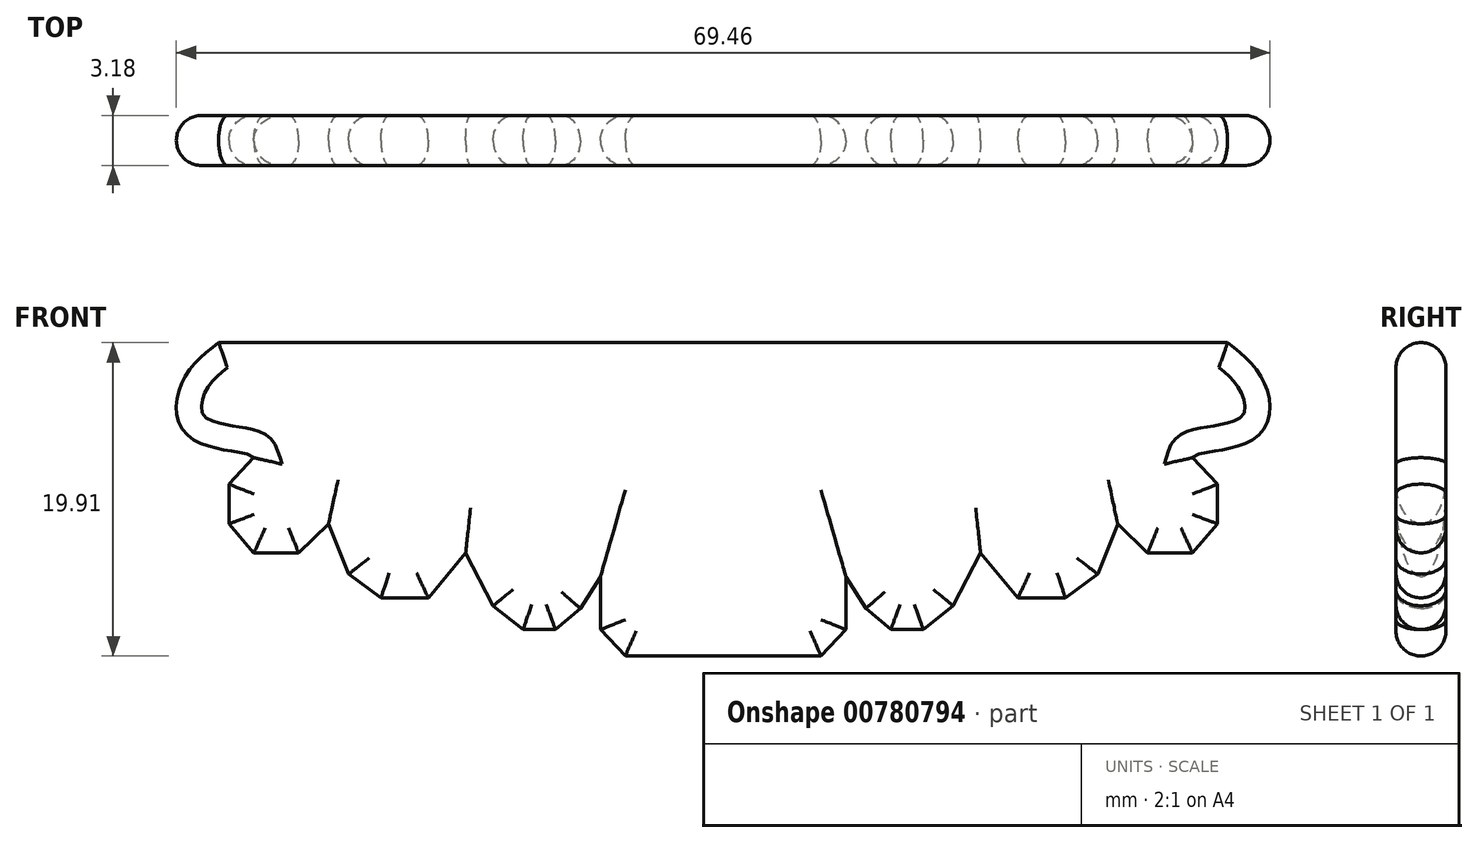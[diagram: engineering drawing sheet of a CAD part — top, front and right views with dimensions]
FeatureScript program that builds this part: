
annotation { "Feature Type Name" : "Feature", "Feature Type Description" : "" }
export const myFeature = defineFeature(function(context is Context, id is Id, definition is map)
    precondition{}
    {
        {
            var Q0;
            Q0=qCreatedBy(makeId("Front.planeOp"),FACE);
            var sketch = newSketch(context, id + "F0", { "sketchPlane" : qUnion([Q0])});
            skLineSegment(sketch, "E0", {"start": v(222.2, -107.52) * mm, "end": v(222.2, 203.58) * mm});
            skLineSegment(sketch, "E1", {"start": v(222.2, 203.58) * mm, "end": v(149.6, 203.58) * mm});
            skLineSegment(sketch, "E2", {"start": v(149.6, 203.58) * mm, "end": v(-239.67, 203.58) * mm});
            skFitSpline(sketch, "E3", {"points": [v(-239.67, 203.58) * mm, v(-277.43, 161.87) * mm, v(-269.83, 108.1) * mm, v(-206.49, 89.28) * mm, v(-203.96, 86.59) * mm], "startDerivative": vector(-149.5, -118.64) * mm, "endDerivative": vector(11.53, -36.45) * mm});
            skLineSegment(sketch, "E4", {"start": v(-203.96, 86.59) * mm, "end": v(-229.3, 59.7) * mm});
            skLineSegment(sketch, "E5", {"start": v(-229.3, 59.7) * mm, "end": v(-229.3, 19.38) * mm});
            skLineSegment(sketch, "E6", {"start": v(-229.3, 19.38) * mm, "end": v(-203.96, -10.2) * mm});
            skLineSegment(sketch, "E7", {"start": v(-203.96, -10.2) * mm, "end": v(-158.35, -10.2) * mm});
            skLineSegment(sketch, "E8", {"start": v(-158.35, -10.2) * mm, "end": v(-127.95, 19.38) * mm});
            skLineSegment(sketch, "E9", {"start": v(-127.95, 19.38) * mm, "end": v(-107.68, -31.7) * mm});
            skLineSegment(sketch, "E10", {"start": v(-107.68, -31.7) * mm, "end": v(-74.74, -55.9) * mm});
            skLineSegment(sketch, "E11", {"start": v(-74.74, -55.9) * mm, "end": v(-26.6, -55.9) * mm});
            skLineSegment(sketch, "E12", {"start": v(-26.6, -55.9) * mm, "end": v(11.4, -10.2) * mm});
            skLineSegment(sketch, "E13", {"start": v(11.4, -10.2) * mm, "end": v(39.28, -63.97) * mm});
            skLineSegment(sketch, "E14", {"start": v(39.28, -63.97) * mm, "end": v(69.68, -88.16) * mm});
            skLineSegment(sketch, "E15", {"start": v(69.68, -88.16) * mm, "end": v(102.62, -88.16) * mm});
            skLineSegment(sketch, "E16", {"start": v(102.62, -88.16) * mm, "end": v(127.95, -66.66) * mm});
            skLineSegment(sketch, "E17", {"start": v(127.95, -66.66) * mm, "end": v(148.22, -34.4) * mm});
            skLineSegment(sketch, "E18", {"start": v(148.22, -34.4) * mm, "end": v(148.22, -88.16) * mm});
            skLineSegment(sketch, "E19", {"start": v(148.22, -88.16) * mm, "end": v(173.56, -115.05) * mm});
            skLineSegment(sketch, "E20", {"start": v(173.56, -115.05) * mm, "end": v(222.2, -115.05) * mm});
            skLineSegment(sketch, "E21", {"start": v(222.2, -115.05) * mm, "end": v(222.2, 203.58) * mm});
            skSolve(sketch);
        }
        {
            var Q0;
            {var subQ0=sQuery(id+"F0.wireOp",EDGE,"E1");Q0=makeQuery(id+"F0.imprint","IMPRINT",FACE,{"disambiguationData":[TD([[makeQuery(id+"F0.imprint","IMPRINT",EDGE,{"derivedFrom":subQ0}),1.0]])]});}
            extrude(context, id + "F1", {"entities" : qUnion([Q0]), "depth" : 50.8 * mm, "offsetDistance" : 25.4 * mm});
        }
        {
            var Q0;
            Q0=makeQuery(id+"F1.opExtrude","SWEPT_FACE",FACE,{"disambiguationData":[OSD([sQuery(id+"F0.wireOp",EDGE,"E21")])]});
            var sketch = newSketch(context, id + "F2", { "sketchPlane" : qUnion([Q0])});
            skLineSegment(sketch, "E22", {"start": v(-50.8, 203.58) * mm, "end": v(-50.8, -115.05) * mm});
            skLineSegment(sketch, "E23", {"start": v(-50.8, -115.05) * mm, "end": v(0, -115.05) * mm});
            skLineSegment(sketch, "E24", {"start": v(0, -115.05) * mm, "end": v(0, 203.58) * mm});
            skLineSegment(sketch, "E25", {"start": v(0, 203.58) * mm, "end": v(-50.8, 203.58) * mm});
            skSolve(sketch);
        }
        {
            var Q0;
            Q0=makeQuery(id+"F2.imprint","IMPRINT",FACE,{"disambiguationData":[TD([[makeQuery(id+"F2.imprint","IMPRINT",EDGE,{"derivedFrom":sQuery(id+"F2.wireOp",EDGE,"E22")}),-1.0]])]});
            extrude(context, id + "F3", {"entities" : qUnion([Q0]), "operationType" : NewBodyOperationType.ADD, "depth" : 50.8 * mm, "offsetDistance" : 25.4 * mm});
        }
        {
            var Q0;
            Q0=makeQuery(id+"F3.boolean.opBoolean","MERGE",EDGE,{"derivedFrom":[makeQuery(id+"F1.opExtrude","CAP_EDGE",EDGE,{"disambiguationData":[OSD([sQuery(id+"F0.wireOp",EDGE,"E1"),sQuery(id+"F0.wireOp",EDGE,"E2")])],"isStart":false}),makeQuery(id+"F3.opExtrude","SWEPT_EDGE",EDGE,{"disambiguationData":[OSD([sQuery(id+"F2.wireOp",EDGE,"E22"),sQuery(id+"F2.wireOp",EDGE,"E25")])]})]});
            var Q1;
            Q1=makeQuery(id+"F1.opExtrude","CAP_EDGE",EDGE,{"disambiguationData":[OSD([sQuery(id+"F0.wireOp",EDGE,"E3")])],"isStart":false});
            var Q2;
            Q2=makeQuery(id+"F1.opExtrude","CAP_EDGE",EDGE,{"disambiguationData":[OSD([sQuery(id+"F0.wireOp",EDGE,"E4")])],"isStart":false});
            var Q3;
            Q3=makeQuery(id+"F1.opExtrude","CAP_EDGE",EDGE,{"disambiguationData":[OSD([sQuery(id+"F0.wireOp",EDGE,"E5")])],"isStart":false});
            var Q4;
            Q4=makeQuery(id+"F1.opExtrude","CAP_EDGE",EDGE,{"disambiguationData":[OSD([sQuery(id+"F0.wireOp",EDGE,"E6")])],"isStart":false});
            var Q5;
            Q5=makeQuery(id+"F1.opExtrude","CAP_EDGE",EDGE,{"disambiguationData":[OSD([sQuery(id+"F0.wireOp",EDGE,"E8")])],"isStart":false});
            var Q6;
            Q6=makeQuery(id+"F1.opExtrude","CAP_EDGE",EDGE,{"disambiguationData":[OSD([sQuery(id+"F0.wireOp",EDGE,"E7")])],"isStart":false});
            var Q7;
            Q7=makeQuery(id+"F1.opExtrude","CAP_EDGE",EDGE,{"disambiguationData":[OSD([sQuery(id+"F0.wireOp",EDGE,"E9")])],"isStart":false});
            var Q8;
            Q8=makeQuery(id+"F1.opExtrude","CAP_EDGE",EDGE,{"disambiguationData":[OSD([sQuery(id+"F0.wireOp",EDGE,"E10")])],"isStart":false});
            var Q9;
            Q9=makeQuery(id+"F1.opExtrude","CAP_EDGE",EDGE,{"disambiguationData":[OSD([sQuery(id+"F0.wireOp",EDGE,"E11")])],"isStart":false});
            var Q10;
            Q10=makeQuery(id+"F1.opExtrude","CAP_EDGE",EDGE,{"disambiguationData":[OSD([sQuery(id+"F0.wireOp",EDGE,"E12")])],"isStart":false});
            var Q11;
            Q11=makeQuery(id+"F1.opExtrude","CAP_EDGE",EDGE,{"disambiguationData":[OSD([sQuery(id+"F0.wireOp",EDGE,"E13")])],"isStart":false});
            var Q12;
            Q12=makeQuery(id+"F1.opExtrude","CAP_EDGE",EDGE,{"disambiguationData":[OSD([sQuery(id+"F0.wireOp",EDGE,"E14")])],"isStart":false});
            var Q13;
            Q13=makeQuery(id+"F1.opExtrude","CAP_EDGE",EDGE,{"disambiguationData":[OSD([sQuery(id+"F0.wireOp",EDGE,"E15")])],"isStart":false});
            var Q14;
            Q14=makeQuery(id+"F1.opExtrude","CAP_EDGE",EDGE,{"disambiguationData":[OSD([sQuery(id+"F0.wireOp",EDGE,"E16")])],"isStart":false});
            var Q15;
            Q15=makeQuery(id+"F3.boolean.opBoolean","MERGE",EDGE,{"derivedFrom":[makeQuery(id+"F1.opExtrude","CAP_EDGE",EDGE,{"disambiguationData":[OSD([sQuery(id+"F0.wireOp",EDGE,"E20")])],"isStart":false}),makeQuery(id+"F3.opExtrude","SWEPT_EDGE",EDGE,{"disambiguationData":[OSD([sQuery(id+"F2.wireOp",EDGE,"E22"),sQuery(id+"F2.wireOp",EDGE,"E23")])]})]});
            var Q16;
            Q16=makeQuery(id+"F1.opExtrude","CAP_EDGE",EDGE,{"disambiguationData":[OSD([sQuery(id+"F0.wireOp",EDGE,"E19")])],"isStart":false});
            var Q17;
            Q17=makeQuery(id+"F1.opExtrude","CAP_EDGE",EDGE,{"disambiguationData":[OSD([sQuery(id+"F0.wireOp",EDGE,"E18")])],"isStart":false});
            var Q18;
            Q18=makeQuery(id+"F1.opExtrude","CAP_EDGE",EDGE,{"disambiguationData":[OSD([sQuery(id+"F0.wireOp",EDGE,"E17")])],"isStart":false});
            fillet(context, id + "F4", {"entities" : qUnion([Q0, Q1, Q2, Q3, Q4, Q5, Q6, Q7, Q8, Q9, Q10, Q11, Q12, Q13, Q14, Q15, Q16, Q17, Q18]), "radius" : 25.4 * mm, "tangentPropagation" : true, "allowEdgeOverflow" : false});
        }
        {
            var Q0;
            Q0=makeQuery(id+"F3.boolean.opBoolean","MERGE",EDGE,{"derivedFrom":[makeQuery(id+"F1.opExtrude","CAP_EDGE",EDGE,{"disambiguationData":[OSD([sQuery(id+"F0.wireOp",EDGE,"E1"),sQuery(id+"F0.wireOp",EDGE,"E2")])],"isStart":true}),makeQuery(id+"F3.opExtrude","SWEPT_EDGE",EDGE,{"disambiguationData":[OSD([sQuery(id+"F2.wireOp",EDGE,"E24"),sQuery(id+"F2.wireOp",EDGE,"E25")])]})]});
            var Q1;
            Q1=makeQuery(id+"F1.opExtrude","CAP_EDGE",EDGE,{"disambiguationData":[OSD([sQuery(id+"F0.wireOp",EDGE,"E3")])],"isStart":true});
            var Q2;
            Q2=makeQuery(id+"F3.boolean.opBoolean","MERGE",EDGE,{"derivedFrom":[makeQuery(id+"F1.opExtrude","CAP_EDGE",EDGE,{"disambiguationData":[OSD([sQuery(id+"F0.wireOp",EDGE,"E20")])],"isStart":true}),makeQuery(id+"F3.opExtrude","SWEPT_EDGE",EDGE,{"disambiguationData":[OSD([sQuery(id+"F2.wireOp",EDGE,"E23"),sQuery(id+"F2.wireOp",EDGE,"E24")])]})]});
            var Q3;
            Q3=makeQuery(id+"F1.opExtrude","CAP_EDGE",EDGE,{"disambiguationData":[OSD([sQuery(id+"F0.wireOp",EDGE,"E19")])],"isStart":true});
            var Q4;
            Q4=makeQuery(id+"F1.opExtrude","CAP_EDGE",EDGE,{"disambiguationData":[OSD([sQuery(id+"F0.wireOp",EDGE,"E18")])],"isStart":true});
            var Q5;
            Q5=makeQuery(id+"F1.opExtrude","CAP_EDGE",EDGE,{"disambiguationData":[OSD([sQuery(id+"F0.wireOp",EDGE,"E17")])],"isStart":true});
            var Q6;
            Q6=makeQuery(id+"F1.opExtrude","CAP_EDGE",EDGE,{"disambiguationData":[OSD([sQuery(id+"F0.wireOp",EDGE,"E16")])],"isStart":true});
            var Q7;
            Q7=makeQuery(id+"F1.opExtrude","CAP_EDGE",EDGE,{"disambiguationData":[OSD([sQuery(id+"F0.wireOp",EDGE,"E15")])],"isStart":true});
            var Q8;
            Q8=makeQuery(id+"F1.opExtrude","CAP_EDGE",EDGE,{"disambiguationData":[OSD([sQuery(id+"F0.wireOp",EDGE,"E14")])],"isStart":true});
            var Q9;
            Q9=makeQuery(id+"F1.opExtrude","CAP_EDGE",EDGE,{"disambiguationData":[OSD([sQuery(id+"F0.wireOp",EDGE,"E13")])],"isStart":true});
            var Q10;
            Q10=makeQuery(id+"F1.opExtrude","CAP_EDGE",EDGE,{"disambiguationData":[OSD([sQuery(id+"F0.wireOp",EDGE,"E12")])],"isStart":true});
            var Q11;
            Q11=makeQuery(id+"F1.opExtrude","CAP_EDGE",EDGE,{"disambiguationData":[OSD([sQuery(id+"F0.wireOp",EDGE,"E11")])],"isStart":true});
            var Q12;
            Q12=makeQuery(id+"F1.opExtrude","CAP_EDGE",EDGE,{"disambiguationData":[OSD([sQuery(id+"F0.wireOp",EDGE,"E4")])],"isStart":true});
            var Q13;
            Q13=makeQuery(id+"F1.opExtrude","CAP_EDGE",EDGE,{"disambiguationData":[OSD([sQuery(id+"F0.wireOp",EDGE,"E5")])],"isStart":true});
            var Q14;
            Q14=makeQuery(id+"F1.opExtrude","CAP_EDGE",EDGE,{"disambiguationData":[OSD([sQuery(id+"F0.wireOp",EDGE,"E6")])],"isStart":true});
            var Q15;
            Q15=makeQuery(id+"F1.opExtrude","CAP_EDGE",EDGE,{"disambiguationData":[OSD([sQuery(id+"F0.wireOp",EDGE,"E7")])],"isStart":true});
            var Q16;
            Q16=makeQuery(id+"F1.opExtrude","CAP_EDGE",EDGE,{"disambiguationData":[OSD([sQuery(id+"F0.wireOp",EDGE,"E8")])],"isStart":true});
            var Q17;
            Q17=makeQuery(id+"F1.opExtrude","CAP_EDGE",EDGE,{"disambiguationData":[OSD([sQuery(id+"F0.wireOp",EDGE,"E9")])],"isStart":true});
            var Q18;
            Q18=makeQuery(id+"F1.opExtrude","CAP_EDGE",EDGE,{"disambiguationData":[OSD([sQuery(id+"F0.wireOp",EDGE,"E10")])],"isStart":true});
            fillet(context, id + "F5", {"entities" : qUnion([Q0, Q1, Q2, Q3, Q4, Q5, Q6, Q7, Q8, Q9, Q10, Q11, Q12, Q13, Q14, Q15, Q16, Q17, Q18]), "radius" : 25.4 * mm, "tangentPropagation" : true, "allowEdgeOverflow" : false});
        }
        {
            var Q0;
            Q0=makeQuery(id+"F1.opExtrude","SWEPT_BODY",BODY,{"disambiguationData":[OSD([sQuery(id+"F0.wireOp",EDGE,"E1"),sQuery(id+"F0.wireOp",EDGE,"E2"),sQuery(id+"F0.wireOp",EDGE,"E3"),sQuery(id+"F0.wireOp",EDGE,"E4"),sQuery(id+"F0.wireOp",EDGE,"E5"),sQuery(id+"F0.wireOp",EDGE,"E6"),sQuery(id+"F0.wireOp",EDGE,"E7"),sQuery(id+"F0.wireOp",EDGE,"E8"),sQuery(id+"F0.wireOp",EDGE,"E9"),sQuery(id+"F0.wireOp",EDGE,"E10"),sQuery(id+"F0.wireOp",EDGE,"E11"),sQuery(id+"F0.wireOp",EDGE,"E12"),sQuery(id+"F0.wireOp",EDGE,"E13"),sQuery(id+"F0.wireOp",EDGE,"E14"),sQuery(id+"F0.wireOp",EDGE,"E15"),sQuery(id+"F0.wireOp",EDGE,"E16"),sQuery(id+"F0.wireOp",EDGE,"E17"),sQuery(id+"F0.wireOp",EDGE,"E18"),sQuery(id+"F0.wireOp",EDGE,"E19"),sQuery(id+"F0.wireOp",EDGE,"E20"),sQuery(id+"F0.wireOp",EDGE,"E21")])]});
            var Q1;
            Q1=makeQuery(id+"F3.opExtrude","CAP_FACE",FACE,{"disambiguationData":[OSD([sQuery(id+"F2.wireOp",EDGE,"E22"),sQuery(id+"F2.wireOp",EDGE,"E23"),sQuery(id+"F2.wireOp",EDGE,"E24"),sQuery(id+"F2.wireOp",EDGE,"E25")])],"isStart":false});
            mirror(context, id + "F6", {"operationType" : NewBodyOperationType.ADD, "entities" : qUnion([Q0]), "mirrorPlane" : qUnion([Q1])});
        }
        {
            var Q0;
            Q0=makeQuery(id+"F1.opExtrude","SWEPT_BODY",BODY,{"disambiguationData":[OSD([sQuery(id+"F0.wireOp",EDGE,"E1"),sQuery(id+"F0.wireOp",EDGE,"E2"),sQuery(id+"F0.wireOp",EDGE,"E3"),sQuery(id+"F0.wireOp",EDGE,"E4"),sQuery(id+"F0.wireOp",EDGE,"E5"),sQuery(id+"F0.wireOp",EDGE,"E6"),sQuery(id+"F0.wireOp",EDGE,"E7"),sQuery(id+"F0.wireOp",EDGE,"E8"),sQuery(id+"F0.wireOp",EDGE,"E9"),sQuery(id+"F0.wireOp",EDGE,"E10"),sQuery(id+"F0.wireOp",EDGE,"E11"),sQuery(id+"F0.wireOp",EDGE,"E12"),sQuery(id+"F0.wireOp",EDGE,"E13"),sQuery(id+"F0.wireOp",EDGE,"E14"),sQuery(id+"F0.wireOp",EDGE,"E15"),sQuery(id+"F0.wireOp",EDGE,"E16"),sQuery(id+"F0.wireOp",EDGE,"E17"),sQuery(id+"F0.wireOp",EDGE,"E18"),sQuery(id+"F0.wireOp",EDGE,"E19"),sQuery(id+"F0.wireOp",EDGE,"E20"),sQuery(id+"F0.wireOp",EDGE,"E21")])]});
            var Q1;
            Q1=qCreatedBy(makeId("Origin.pointOp"),VERTEX);
            transform(context, id + "F7", {"entities" : qUnion([Q0]), "transformType" : TransformType.SCALE_UNIFORMLY, "scale" : .5, "scalePoint" : qUnion([Q1]), "makeCopy" : false});
        }
        {
            var Q0;
            Q0=makeQuery(id+"F1.opExtrude","SWEPT_BODY",BODY,{"disambiguationData":[OSD([sQuery(id+"F0.wireOp",EDGE,"E1"),sQuery(id+"F0.wireOp",EDGE,"E2"),sQuery(id+"F0.wireOp",EDGE,"E3"),sQuery(id+"F0.wireOp",EDGE,"E4"),sQuery(id+"F0.wireOp",EDGE,"E5"),sQuery(id+"F0.wireOp",EDGE,"E6"),sQuery(id+"F0.wireOp",EDGE,"E7"),sQuery(id+"F0.wireOp",EDGE,"E8"),sQuery(id+"F0.wireOp",EDGE,"E9"),sQuery(id+"F0.wireOp",EDGE,"E10"),sQuery(id+"F0.wireOp",EDGE,"E11"),sQuery(id+"F0.wireOp",EDGE,"E12"),sQuery(id+"F0.wireOp",EDGE,"E13"),sQuery(id+"F0.wireOp",EDGE,"E14"),sQuery(id+"F0.wireOp",EDGE,"E15"),sQuery(id+"F0.wireOp",EDGE,"E16"),sQuery(id+"F0.wireOp",EDGE,"E17"),sQuery(id+"F0.wireOp",EDGE,"E18"),sQuery(id+"F0.wireOp",EDGE,"E19"),sQuery(id+"F0.wireOp",EDGE,"E20"),sQuery(id+"F0.wireOp",EDGE,"E21")])]});
            var Q1;
            Q1=qCreatedBy(makeId("Origin.pointOp"),VERTEX);
            transform(context, id + "F8", {"entities" : qUnion([Q0]), "transformType" : TransformType.SCALE_UNIFORMLY, "scale" : .25, "scalePoint" : qUnion([Q1]), "makeCopy" : false});
        }
        {
            var Q0;
            Q0=makeQuery(id+"F1.opExtrude","SWEPT_BODY",BODY,{"disambiguationData":[OSD([sQuery(id+"F0.wireOp",EDGE,"E1"),sQuery(id+"F0.wireOp",EDGE,"E2"),sQuery(id+"F0.wireOp",EDGE,"E3"),sQuery(id+"F0.wireOp",EDGE,"E4"),sQuery(id+"F0.wireOp",EDGE,"E5"),sQuery(id+"F0.wireOp",EDGE,"E6"),sQuery(id+"F0.wireOp",EDGE,"E7"),sQuery(id+"F0.wireOp",EDGE,"E8"),sQuery(id+"F0.wireOp",EDGE,"E9"),sQuery(id+"F0.wireOp",EDGE,"E10"),sQuery(id+"F0.wireOp",EDGE,"E11"),sQuery(id+"F0.wireOp",EDGE,"E12"),sQuery(id+"F0.wireOp",EDGE,"E13"),sQuery(id+"F0.wireOp",EDGE,"E14"),sQuery(id+"F0.wireOp",EDGE,"E15"),sQuery(id+"F0.wireOp",EDGE,"E16"),sQuery(id+"F0.wireOp",EDGE,"E17"),sQuery(id+"F0.wireOp",EDGE,"E18"),sQuery(id+"F0.wireOp",EDGE,"E19"),sQuery(id+"F0.wireOp",EDGE,"E20"),sQuery(id+"F0.wireOp",EDGE,"E21")])]});
            var Q1;
            Q1=qCreatedBy(makeId("Origin.pointOp"),VERTEX);
            transform(context, id + "F9", {"entities" : qUnion([Q0]), "transformType" : TransformType.SCALE_UNIFORMLY, "scale" : .5, "scalePoint" : qUnion([Q1]), "makeCopy" : false});
        }
    });
